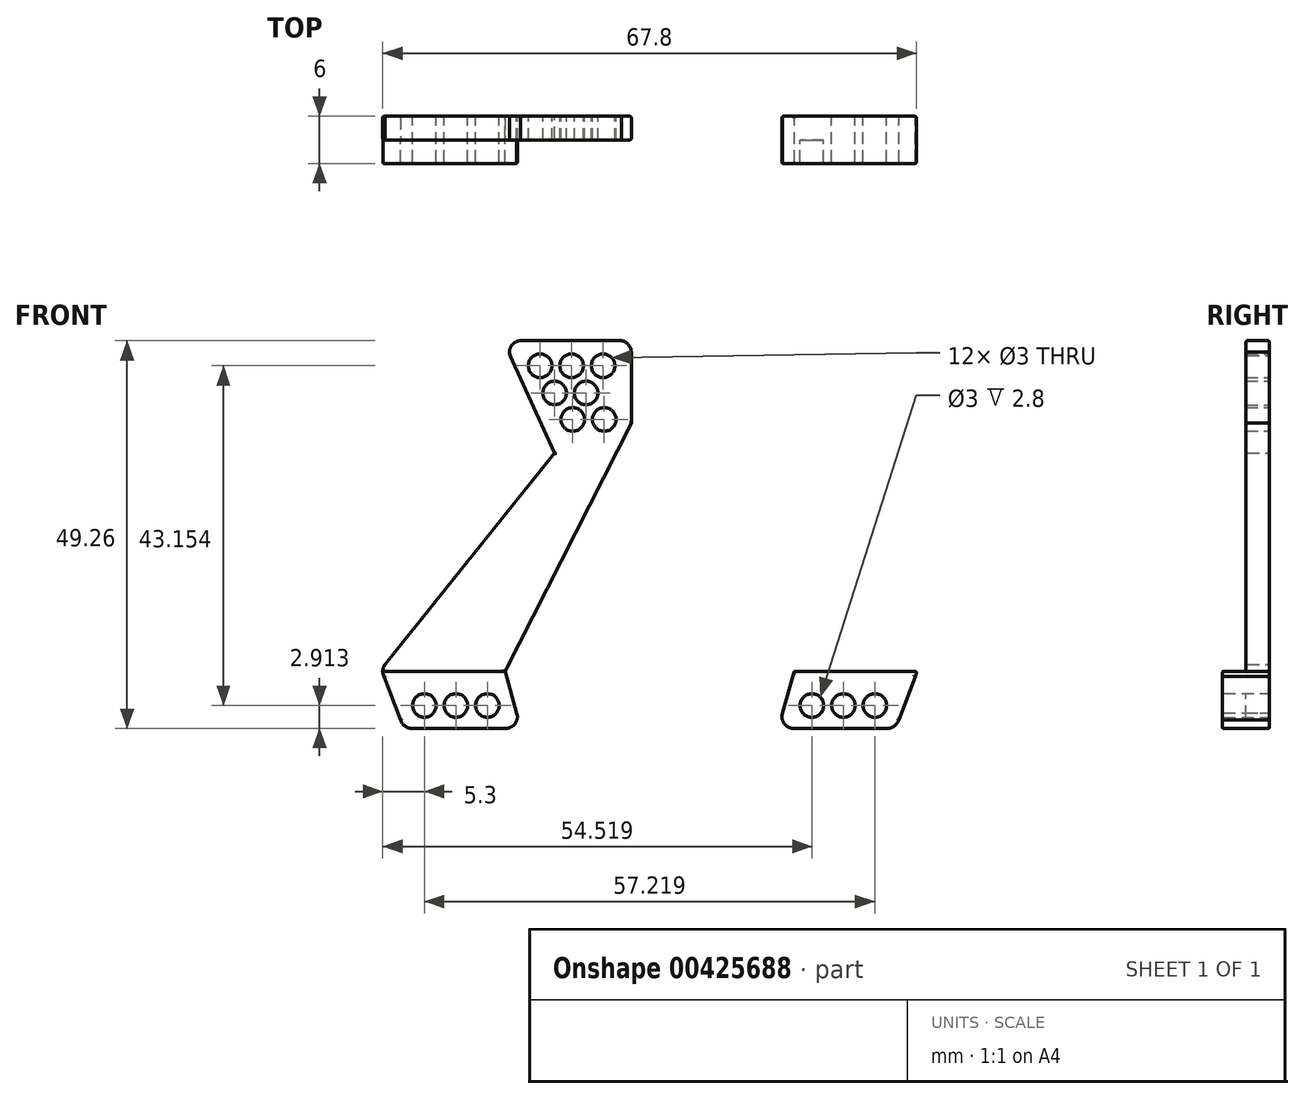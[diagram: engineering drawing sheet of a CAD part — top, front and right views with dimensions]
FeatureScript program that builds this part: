
annotation { "Feature Type Name" : "Feature", "Feature Type Description" : "" }
export const myFeature = defineFeature(function(context is Context, id is Id, definition is map)
    precondition{}
    {
        {
            var Q0;
            Q0=qCreatedBy(makeId("Front.planeOp"),FACE);
            var sketch = newSketch(context, id + "F0", { "sketchPlane" : qUnion([Q0])});
            skCircle(sketch, "E0", {"center": v(18.99, 2.93) * mm, "radius": 1.5 * mm});
            skCircle(sketch, "E1", {"center": v(22.99, 2.93) * mm, "radius": 1.5 * mm});
            skCircle(sketch, "E2", {"center": v(26.99, 2.93) * mm, "radius": 1.5 * mm});
            skCircle(sketch, "E3", {"center": v(4.3, 46.09) * mm, "radius": 1.5 * mm});
            skCircle(sketch, "E4", {"center": v(8.3, 46.09) * mm, "radius": 1.5 * mm});
            skCircle(sketch, "E5", {"center": v(12.3, 46.09) * mm, "radius": 1.5 * mm});
            skCircle(sketch, "E6", {"center": v(6.45, 42.63) * mm, "radius": 1.5 * mm});
            skCircle(sketch, "E7", {"center": v(10.45, 42.63) * mm, "radius": 1.5 * mm});
            skCircle(sketch, "E8", {"center": v(4.15, 39.27) * mm, "radius": 1.5 * mm});
            skCircle(sketch, "E9", {"center": v(8.15, 39.27) * mm, "radius": 1.5 * mm});
            skLineSegment(sketch, "E10", {"start": v(16.59, 0.02) * mm, "end": v(28.58, 0.02) * mm});
            skLineSegment(sketch, "E11", {"start": v(32, 8.18) * mm, "end": v(10.47, 34.98) * mm});
            skLineSegment(sketch, "E12", {"start": v(16.14, 47.39) * mm, "end": v(10.47, 34.98) * mm});
            skLineSegment(sketch, "E13", {"start": v(14.78, 49.28) * mm, "end": v(1.96, 49.28) * mm});
            skLineSegment(sketch, "E14", {"start": v(0.71, 47.83) * mm, "end": v(0.71, 38.84) * mm});
            skLineSegment(sketch, "E15", {"start": v(0.71, 38.84) * mm, "end": v(16.72, 7.29) * mm});
            skLineSegment(sketch, "E16", {"start": v(16.72, 7.29) * mm, "end": v(15.21, 1.82) * mm});
            skLineSegment(sketch, "E17", {"start": v(32.14, 6.64) * mm, "end": v(29.94, 0.89) * mm});
            skArc(sketch, "E18", {"start": v(32.14, 6.64) * mm, "mid": v(32.28, 7.43) * mm, "end": v(32, 8.18) * mm});
            skArc(sketch, "E19", {"start": v(28.58, 0.02) * mm, "mid": v(29.47, 0.32) * mm, "end": v(30.02, 1.1) * mm});
            skArc(sketch, "E20", {"start": v(15.27, 2.02) * mm, "mid": v(15.48, 0.62) * mm, "end": v(16.77, 0.02) * mm});
            skArc(sketch, "E21", {"start": v(1.97, 49.29) * mm, "mid": v(1.06, 48.77) * mm, "end": v(0.71, 47.78) * mm});
            skArc(sketch, "E22", {"start": v(16.14, 47.38) * mm, "mid": v(15.91, 48.66) * mm, "end": v(14.78, 49.28) * mm});
            skCircle(sketch, "E23", {"center": v(-22.23, 2.93) * mm, "radius": 1.5 * mm});
            skCircle(sketch, "E24", {"center": v(-26.23, 2.93) * mm, "radius": 1.5 * mm});
            skCircle(sketch, "E25", {"center": v(-30.23, 2.93) * mm, "radius": 1.5 * mm});
            skCircle(sketch, "E26", {"center": v(-7.53, 46.09) * mm, "radius": 1.5 * mm});
            skCircle(sketch, "E27", {"center": v(-11.53, 46.09) * mm, "radius": 1.5 * mm});
            skCircle(sketch, "E28", {"center": v(-15.53, 46.09) * mm, "radius": 1.5 * mm});
            skCircle(sketch, "E29", {"center": v(-9.69, 42.63) * mm, "radius": 1.5 * mm});
            skCircle(sketch, "E30", {"center": v(-13.69, 42.63) * mm, "radius": 1.5 * mm});
            skCircle(sketch, "E31", {"center": v(-7.4, 39.27) * mm, "radius": 1.5 * mm});
            skCircle(sketch, "E32", {"center": v(-11.4, 39.27) * mm, "radius": 1.5 * mm});
            skLineSegment(sketch, "E33", {"start": v(-19.83, 0.02) * mm, "end": v(-31.82, 0.02) * mm});
            skLineSegment(sketch, "E34", {"start": v(-35.23, 8.18) * mm, "end": v(-13.71, 34.98) * mm});
            skLineSegment(sketch, "E35", {"start": v(-19.38, 47.39) * mm, "end": v(-13.71, 34.98) * mm});
            skLineSegment(sketch, "E36", {"start": v(-18.02, 49.28) * mm, "end": v(-5.2, 49.28) * mm});
            skLineSegment(sketch, "E37", {"start": v(-3.96, 47.83) * mm, "end": v(-3.96, 38.84) * mm});
            skLineSegment(sketch, "E38", {"start": v(-3.96, 38.84) * mm, "end": v(-19.97, 7.29) * mm});
            skLineSegment(sketch, "E39", {"start": v(-19.97, 7.29) * mm, "end": v(-18.45, 1.82) * mm});
            skLineSegment(sketch, "E40", {"start": v(-35.38, 6.64) * mm, "end": v(-33.18, 0.89) * mm});
            skArc(sketch, "E41", {"start": v(-35.38, 6.64) * mm, "mid": v(-35.52, 7.43) * mm, "end": v(-35.23, 8.18) * mm});
            skArc(sketch, "E42", {"start": v(-31.82, 0.02) * mm, "mid": v(-32.72, 0.32) * mm, "end": v(-33.26, 1.1) * mm});
            skArc(sketch, "E43", {"start": v(-18.5, 2.02) * mm, "mid": v(-18.73, 0.62) * mm, "end": v(-20.01, 0.02) * mm});
            skArc(sketch, "E44", {"start": v(-5.2, 49.29) * mm, "mid": v(-4.3, 48.77) * mm, "end": v(-3.96, 47.78) * mm});
            skArc(sketch, "E45", {"start": v(-19.38, 47.38) * mm, "mid": v(-19.15, 48.66) * mm, "end": v(-18.02, 49.28) * mm});
            skSolve(sketch);
        }
        {
            var Q0;
            Q0=qCreatedBy(makeId("Front.planeOp"),FACE);
            var sketch = newSketch(context, id + "F1", { "sketchPlane" : qUnion([Q0])});
            skCircle(sketch, "E46", {"center": v(18.99, 2.93) * mm, "radius": 1.5 * mm});
            skCircle(sketch, "E47", {"center": v(22.99, 2.93) * mm, "radius": 1.5 * mm});
            skCircle(sketch, "E48", {"center": v(26.99, 2.93) * mm, "radius": 1.5 * mm});
            skLineSegment(sketch, "E49", {"start": v(16.59, 0.02) * mm, "end": v(28.58, 0.02) * mm});
            skLineSegment(sketch, "E50", {"start": v(16.72, 7.29) * mm, "end": v(15.21, 1.82) * mm});
            skLineSegment(sketch, "E51", {"start": v(32.14, 6.64) * mm, "end": v(29.94, 0.89) * mm});
            skArc(sketch, "E52", {"start": v(32.14, 6.64) * mm, "mid": v(32.25, 6.95) * mm, "end": v(32.28, 7.29) * mm});
            skArc(sketch, "E53", {"start": v(28.58, 0.02) * mm, "mid": v(29.47, 0.32) * mm, "end": v(30.02, 1.1) * mm});
            skArc(sketch, "E54", {"start": v(15.27, 2.02) * mm, "mid": v(15.48, 0.62) * mm, "end": v(16.77, 0.02) * mm});
            skCircle(sketch, "E55", {"center": v(-22.23, 2.93) * mm, "radius": 1.5 * mm});
            skCircle(sketch, "E56", {"center": v(-26.23, 2.93) * mm, "radius": 1.5 * mm});
            skCircle(sketch, "E57", {"center": v(-30.23, 2.93) * mm, "radius": 1.5 * mm});
            skLineSegment(sketch, "E58", {"start": v(-19.83, 0.02) * mm, "end": v(-31.82, 0.02) * mm});
            skLineSegment(sketch, "E59", {"start": v(-19.97, 7.29) * mm, "end": v(-18.45, 1.82) * mm});
            skLineSegment(sketch, "E60", {"start": v(-35.38, 6.64) * mm, "end": v(-33.18, 0.89) * mm});
            skArc(sketch, "E61", {"start": v(-35.38, 6.64) * mm, "mid": v(-35.49, 6.95) * mm, "end": v(-35.53, 7.29) * mm});
            skArc(sketch, "E62", {"start": v(-31.82, 0.02) * mm, "mid": v(-32.71, 0.32) * mm, "end": v(-33.26, 1.1) * mm});
            skArc(sketch, "E63", {"start": v(-18.5, 2.02) * mm, "mid": v(-18.73, 0.62) * mm, "end": v(-20.01, 0.02) * mm});
            skLineSegment(sketch, "E64", {"start": v(-19.97, 7.29) * mm, "end": v(-35.53, 7.29) * mm});
            skLineSegment(sketch, "E65", {"start": v(16.72, 7.29) * mm, "end": v(32.28, 7.29) * mm});
            skSolve(sketch);
        }
        {
            var Q0;
            Q0 = qSketchRegion(id + "F1", true);
            extrude(context, id + "F2", {"entities" : qUnion([Q0]), "depth" : 6 * mm});
        }
        {
            var Q0;
            Q0=makeQuery(id+"F0.imprint","IMPRINT",FACE,{"disambiguationData":[TD([[makeQuery(id+"F0.imprint","IMPRINT",EDGE,{"derivedFrom":sQuery(id+"F0.wireOp",EDGE,"E23")}),-1.0]])]});
            var Q1;
            Q1=makeQuery(id+"F0.imprint","IMPRINT",FACE,{"disambiguationData":[TD([[makeQuery(id+"F0.imprint","IMPRINT",EDGE,{"derivedFrom":sQuery(id+"F0.wireOp",EDGE,"E0")}),1.0]])]});
            extrude(context, id + "F3", {"entities" : qUnion([Q0, Q1]), "operationType" : NewBodyOperationType.ADD, "depth" : 3 * mm});
        }
        {
            var Q0;
            Q0=makeQuery(id+"F3.boolean.opBoolean","MERGE",FACE,{"derivedFrom":[makeQuery(id+"F2.opExtrude","CAP_FACE",FACE,{"disambiguationData":[OSD([sQuery(id+"F1.wireOp",EDGE,"E46"),sQuery(id+"F1.wireOp",EDGE,"E47"),sQuery(id+"F1.wireOp",EDGE,"E48"),sQuery(id+"F1.wireOp",EDGE,"E49"),sQuery(id+"F1.wireOp",EDGE,"E50"),sQuery(id+"F1.wireOp",EDGE,"E51"),sQuery(id+"F1.wireOp",EDGE,"E52"),sQuery(id+"F1.wireOp",EDGE,"E53"),sQuery(id+"F1.wireOp",EDGE,"E54"),sQuery(id+"F1.wireOp",EDGE,"E65")])],"isStart":true}),makeQuery(id+"F3.opExtrude","CAP_FACE",FACE,{"disambiguationData":[OSD([sQuery(id+"F0.wireOp",EDGE,"E0"),sQuery(id+"F0.wireOp",EDGE,"E1"),sQuery(id+"F0.wireOp",EDGE,"E2"),sQuery(id+"F0.wireOp",EDGE,"E3"),sQuery(id+"F0.wireOp",EDGE,"E4"),sQuery(id+"F0.wireOp",EDGE,"E5"),sQuery(id+"F0.wireOp",EDGE,"E6"),sQuery(id+"F0.wireOp",EDGE,"E7"),sQuery(id+"F0.wireOp",EDGE,"E8"),sQuery(id+"F0.wireOp",EDGE,"E9"),sQuery(id+"F0.wireOp",EDGE,"E10"),sQuery(id+"F0.wireOp",EDGE,"E11"),sQuery(id+"F0.wireOp",EDGE,"E12"),sQuery(id+"F0.wireOp",EDGE,"E13"),sQuery(id+"F0.wireOp",EDGE,"E14"),sQuery(id+"F0.wireOp",EDGE,"E15"),sQuery(id+"F0.wireOp",EDGE,"E16"),sQuery(id+"F0.wireOp",EDGE,"E17"),sQuery(id+"F0.wireOp",EDGE,"E18"),sQuery(id+"F0.wireOp",EDGE,"E19"),sQuery(id+"F0.wireOp",EDGE,"E20"),sQuery(id+"F0.wireOp",EDGE,"E21"),sQuery(id+"F0.wireOp",EDGE,"E22")])],"isStart":true})]});
            var Q1;
            Q1=makeQuery(id+"F3.boolean.opBoolean","MERGE",FACE,{"derivedFrom":[makeQuery(id+"F2.opExtrude","CAP_FACE",FACE,{"disambiguationData":[OSD([sQuery(id+"F1.wireOp",EDGE,"E55"),sQuery(id+"F1.wireOp",EDGE,"E56"),sQuery(id+"F1.wireOp",EDGE,"E57"),sQuery(id+"F1.wireOp",EDGE,"E58"),sQuery(id+"F1.wireOp",EDGE,"E59"),sQuery(id+"F1.wireOp",EDGE,"E60"),sQuery(id+"F1.wireOp",EDGE,"E61"),sQuery(id+"F1.wireOp",EDGE,"E62"),sQuery(id+"F1.wireOp",EDGE,"E63"),sQuery(id+"F1.wireOp",EDGE,"E64")])],"isStart":true}),makeQuery(id+"F3.opExtrude","CAP_FACE",FACE,{"disambiguationData":[OSD([sQuery(id+"F0.wireOp",EDGE,"E23"),sQuery(id+"F0.wireOp",EDGE,"E24"),sQuery(id+"F0.wireOp",EDGE,"E25"),sQuery(id+"F0.wireOp",EDGE,"E26"),sQuery(id+"F0.wireOp",EDGE,"E27"),sQuery(id+"F0.wireOp",EDGE,"E28"),sQuery(id+"F0.wireOp",EDGE,"E29"),sQuery(id+"F0.wireOp",EDGE,"E30"),sQuery(id+"F0.wireOp",EDGE,"E31"),sQuery(id+"F0.wireOp",EDGE,"E32"),sQuery(id+"F0.wireOp",EDGE,"E33"),sQuery(id+"F0.wireOp",EDGE,"E34"),sQuery(id+"F0.wireOp",EDGE,"E35"),sQuery(id+"F0.wireOp",EDGE,"E36"),sQuery(id+"F0.wireOp",EDGE,"E37"),sQuery(id+"F0.wireOp",EDGE,"E38"),sQuery(id+"F0.wireOp",EDGE,"E39"),sQuery(id+"F0.wireOp",EDGE,"E40"),sQuery(id+"F0.wireOp",EDGE,"E41"),sQuery(id+"F0.wireOp",EDGE,"E42"),sQuery(id+"F0.wireOp",EDGE,"E43"),sQuery(id+"F0.wireOp",EDGE,"E44"),sQuery(id+"F0.wireOp",EDGE,"E45")])],"isStart":true})]});
            fillet(context, id + "F4", {"entities" : qUnion([Q0, Q1]), "radius" : .2 * mm, "tangentPropagation" : true, "allowEdgeOverflow" : false});
        }
        {
            var Q0;
            Q0=makeQuery(id+"F2.opExtrude","CAP_FACE",FACE,{"disambiguationData":[OSD([sQuery(id+"F1.wireOp",EDGE,"E46"),sQuery(id+"F1.wireOp",EDGE,"E47"),sQuery(id+"F1.wireOp",EDGE,"E48"),sQuery(id+"F1.wireOp",EDGE,"E49"),sQuery(id+"F1.wireOp",EDGE,"E50"),sQuery(id+"F1.wireOp",EDGE,"E51"),sQuery(id+"F1.wireOp",EDGE,"E52"),sQuery(id+"F1.wireOp",EDGE,"E53"),sQuery(id+"F1.wireOp",EDGE,"E54"),sQuery(id+"F1.wireOp",EDGE,"E65")])],"isStart":false});
            var Q1;
            Q1=makeQuery(id+"F2.opExtrude","CAP_FACE",FACE,{"disambiguationData":[OSD([sQuery(id+"F1.wireOp",EDGE,"E55"),sQuery(id+"F1.wireOp",EDGE,"E56"),sQuery(id+"F1.wireOp",EDGE,"E57"),sQuery(id+"F1.wireOp",EDGE,"E58"),sQuery(id+"F1.wireOp",EDGE,"E59"),sQuery(id+"F1.wireOp",EDGE,"E60"),sQuery(id+"F1.wireOp",EDGE,"E61"),sQuery(id+"F1.wireOp",EDGE,"E62"),sQuery(id+"F1.wireOp",EDGE,"E63"),sQuery(id+"F1.wireOp",EDGE,"E64")])],"isStart":false});
            var Q2;
            Q2=makeQuery(id+"F3.opExtrude","CAP_EDGE",EDGE,{"disambiguationData":[OSD([sQuery(id+"F0.wireOp",EDGE,"E38")])],"isStart":false});
            var Q3;
            Q3=makeQuery(id+"F3.opExtrude","CAP_EDGE",EDGE,{"disambiguationData":[OSD([sQuery(id+"F0.wireOp",EDGE,"E37")])],"isStart":false});
            var Q4;
            Q4=makeQuery(id+"F3.opExtrude","CAP_EDGE",EDGE,{"disambiguationData":[OSD([sQuery(id+"F0.wireOp",EDGE,"E44")])],"isStart":false});
            var Q5;
            Q5=makeQuery(id+"F3.opExtrude","CAP_EDGE",EDGE,{"disambiguationData":[OSD([sQuery(id+"F0.wireOp",EDGE,"E36")])],"isStart":false});
            var Q6;
            Q6=makeQuery(id+"F3.opExtrude","CAP_EDGE",EDGE,{"disambiguationData":[OSD([sQuery(id+"F0.wireOp",EDGE,"E45")])],"isStart":false});
            var Q7;
            Q7=makeQuery(id+"F3.opExtrude","CAP_EDGE",EDGE,{"disambiguationData":[OSD([sQuery(id+"F0.wireOp",EDGE,"E35")])],"isStart":false});
            var Q8;
            Q8=makeQuery(id+"F3.opExtrude","CAP_EDGE",EDGE,{"disambiguationData":[OSD([sQuery(id+"F0.wireOp",EDGE,"E34")])],"isStart":false});
            var Q9;
            Q9=makeQuery(id+"F3.opExtrude","CAP_EDGE",EDGE,{"disambiguationData":[OSD([sQuery(id+"F0.wireOp",EDGE,"E41")])],"isStart":false});
            var Q10;
            {var subQ0=sQuery(id+"F1.wireOp",EDGE,"E61");var subQ1=sQuery(id+"F1.wireOp",EDGE,"E64");Q10=makeQuery(id+"F3.boolean.opBoolean","SPLIT",EDGE,{"disambiguationData":[topologyDisambiguationEdgeConnected([makeQuery(id+"F2.opExtrude","SWEPT_FACE",FACE,{"disambiguationData":[OSD([subQ1])]})])],"derivedFrom":makeQuery(id+"F2.opExtrude","SWEPT_EDGE",EDGE,{"disambiguationData":[OSD([subQ0,subQ1])]})});}
            var Q11;
            Q11=makeQuery(id+"F3.opExtrude","CAP_EDGE",EDGE,{"disambiguationData":[OSD([sQuery(id+"F0.wireOp",EDGE,"E21")])],"isStart":false});
            var Q12;
            Q12=makeQuery(id+"F3.opExtrude","CAP_EDGE",EDGE,{"disambiguationData":[OSD([sQuery(id+"F0.wireOp",EDGE,"E13")])],"isStart":false});
            var Q13;
            Q13=makeQuery(id+"F3.opExtrude","CAP_EDGE",EDGE,{"disambiguationData":[OSD([sQuery(id+"F0.wireOp",EDGE,"E22")])],"isStart":false});
            var Q14;
            Q14=makeQuery(id+"F3.opExtrude","CAP_EDGE",EDGE,{"disambiguationData":[OSD([sQuery(id+"F0.wireOp",EDGE,"E12")])],"isStart":false});
            var Q15;
            Q15=makeQuery(id+"F3.opExtrude","CAP_EDGE",EDGE,{"disambiguationData":[OSD([sQuery(id+"F0.wireOp",EDGE,"E14")])],"isStart":false});
            var Q16;
            Q16=makeQuery(id+"F3.opExtrude","CAP_EDGE",EDGE,{"disambiguationData":[OSD([sQuery(id+"F0.wireOp",EDGE,"E15")])],"isStart":false});
            var Q17;
            Q17=makeQuery(id+"F3.opExtrude","CAP_EDGE",EDGE,{"disambiguationData":[OSD([sQuery(id+"F0.wireOp",EDGE,"E11")])],"isStart":false});
            var Q18;
            Q18=makeQuery(id+"F3.opExtrude","CAP_EDGE",EDGE,{"disambiguationData":[OSD([sQuery(id+"F0.wireOp",EDGE,"E18")])],"isStart":false});
            var Q19;
            {var subQ0=sQuery(id+"F1.wireOp",EDGE,"E52");var subQ1=sQuery(id+"F1.wireOp",EDGE,"E65");Q19=makeQuery(id+"F3.boolean.opBoolean","SPLIT",EDGE,{"disambiguationData":[topologyDisambiguationEdgeConnected([makeQuery(id+"F2.opExtrude","SWEPT_FACE",FACE,{"disambiguationData":[OSD([subQ1])]})])],"derivedFrom":makeQuery(id+"F2.opExtrude","SWEPT_EDGE",EDGE,{"disambiguationData":[OSD([subQ0,subQ1])]})});}
            fillet(context, id + "F5", {"entities" : qUnion([Q0, Q1, Q2, Q3, Q4, Q5, Q6, Q7, Q8, Q9, Q10, Q11, Q12, Q13, Q14, Q15, Q16, Q17, Q18, Q19]), "radius" : .2 * mm, "tangentPropagation" : true, "allowEdgeOverflow" : false});
        }
        {
            var Q0;
            Q0=makeQuery(id+"F3.boolean.opBoolean","SPLIT",EDGE,{"derivedFrom":makeQuery(id+"F2.opExtrude","SWEPT_EDGE",EDGE,{"disambiguationData":[OSD([sQuery(id+"F1.wireOp",EDGE,"E59"),sQuery(id+"F1.wireOp",EDGE,"E64")])]})});
            fillet(context, id + "F6", {"entities" : qUnion([Q0]), "radius" : .2 * mm, "tangentPropagation" : true, "allowEdgeOverflow" : false});
        }
        {
            var Q0;
            Q0=makeQuery(id+"F3.boolean.opBoolean","SPLIT",EDGE,{"derivedFrom":makeQuery(id+"F2.opExtrude","SWEPT_EDGE",EDGE,{"disambiguationData":[OSD([sQuery(id+"F1.wireOp",EDGE,"E50"),sQuery(id+"F1.wireOp",EDGE,"E65")])]})});
            fillet(context, id + "F7", {"entities" : qUnion([Q0]), "radius" : .2 * mm, "tangentPropagation" : true, "allowEdgeOverflow" : false});
        }
    });
